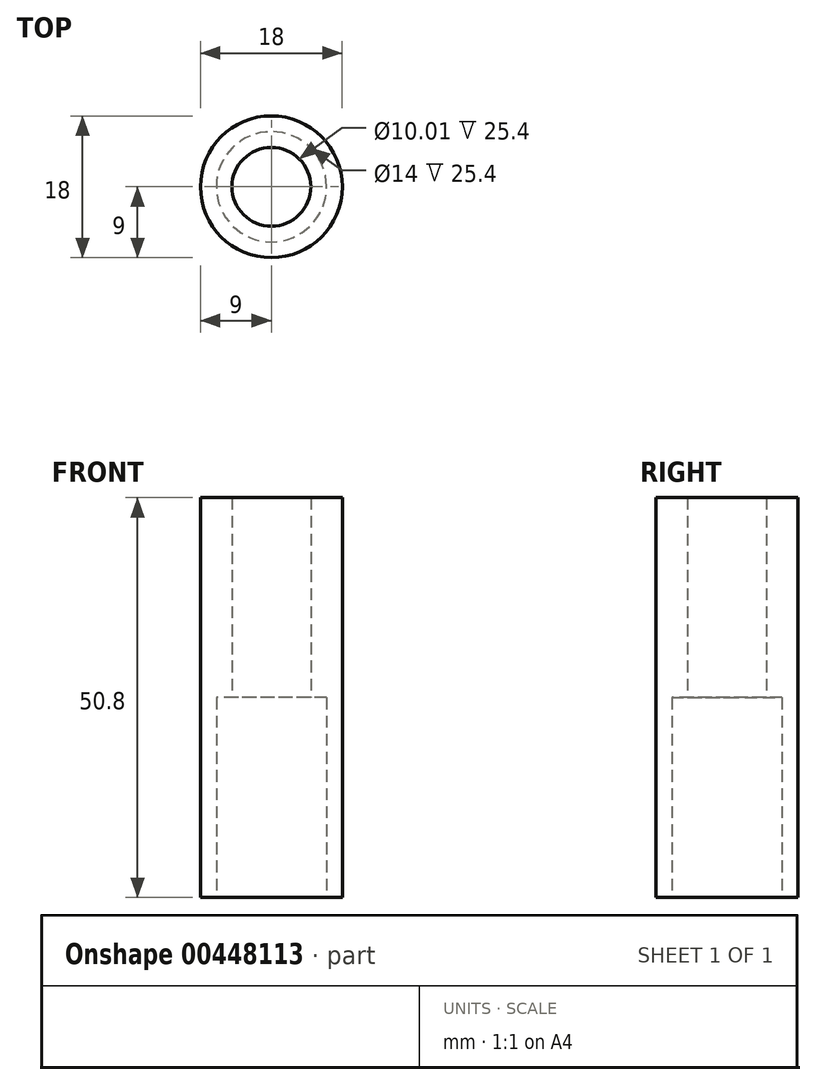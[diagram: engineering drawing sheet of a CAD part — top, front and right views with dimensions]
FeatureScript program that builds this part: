
annotation { "Feature Type Name" : "Feature", "Feature Type Description" : "" }
export const myFeature = defineFeature(function(context is Context, id is Id, definition is map)
    precondition{}
    {
        {
            var Q0;
            Q0=qCreatedBy(makeId("Top.planeOp"),FACE);
            var sketch = newSketch(context, id + "F0", { "sketchPlane" : qUnion([Q0])});
            skCircle(sketch, "E0", {"center": v(0, 0) * mm, "radius": 9 * mm});
            skSolve(sketch);
        }
        {
            var Q0;
            Q0=makeQuery(id+"F0.imprint","IMPRINT",FACE,{"disambiguationData":[TD([[makeQuery(id+"F0.imprint","IMPRINT",EDGE,{"derivedFrom":sQuery(id+"F0.wireOp",EDGE,"E0")}),1.0]])]});
            extrude(context, id + "F1", {"entities" : qUnion([Q0]), "depth" : 50.8 * mm});
        }
        {
            var Q0;
            Q0=qCreatedBy(makeId("Top.planeOp"),FACE);
            var sketch = newSketch(context, id + "F2", { "sketchPlane" : qUnion([Q0])});
            skCircle(sketch, "E1", {"center": v(0, 0) * mm, "radius": 5 * mm});
            skSolve(sketch);
        }
        {
            var Q0;
            Q0 = qSketchRegion(id + "F2", true);
            extrude(context, id + "F3", {"entities" : qUnion([Q0]), "operationType" : NewBodyOperationType.REMOVE, "depth" : 85.1 * mm, "hasSecondDirection" : true, "secondDirectionOppositeDirection" : true, "secondDirectionDepth" : 25.4 * mm});
        }
        {
            var Q0;
            Q0=qCreatedBy(makeId("Top.planeOp"),FACE);
            var sketch = newSketch(context, id + "F4", { "sketchPlane" : qUnion([Q0])});
            skCircle(sketch, "E2", {"center": v(0, 0) * mm, "radius": 7 * mm});
            skSolve(sketch);
        }
        {
            var Q0;
            Q0 = qSketchRegion(id + "F4", true);
            extrude(context, id + "F5", {"entities" : qUnion([Q0]), "operationType" : NewBodyOperationType.REMOVE, "depth" : 25.4 * mm});
        }
    });
